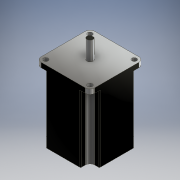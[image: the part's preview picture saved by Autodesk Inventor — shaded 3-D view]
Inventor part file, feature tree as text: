
AUTODESK INVENTOR PART (.ipt)
format: ipt  version: 2017 (Build 210142000, 142)  size: 271,360 bytes
history: native  units: mm
features: extrude x6, sketch x6, projected_geometry x2
ambient origin geometry x8: Origin, YZ Plane, XZ Plane, XY Plane, X Axis, Y Axis, Z Axis, Center Point
bodies: Solid1 (feature_tree)
feature tree (14):
  extrude  "Extrusion1"  Depth=28.5mm
  extrude  "Extrusion2"  Depth=10.0mm
  extrude  "Extrusion3"  Depth=10.0mm
  extrude  "Extrusion4"  Depth=57.0mm
  extrude  "Extrusion5"  Depth=1.0mm TaperAngle=0.0deg
  extrude  "Extrusion6"  Depth=10.0mm TaperAngle=0.0deg
  sketch  "Sketch1"  dims[d2=28.5mm d3=28.5mm]
  sketch  "Sketch2"  dims[d4=10.0mm d5=10.0mm]
  projected_geometry  "Projected Loop1"
  sketch  "Sketch3"  dims[d6=10.0mm d7=10.0mm]
  projected_geometry  "Projected Loop2"
  sketch  "Sketch4"  dims[d8=57.0mm d9=57.0mm]
  sketch  "Sketch5"  dims[d10=1.0mm d11=15.0mm d12=0.0mm]
  sketch  "Sketch6"  dims[d13=46.0mm d14=0.0mm d15=10.0mm d16=0.0mm d17=57.0mm d18=10.0mm d19=10.0mm d20=10.0mm d21=10.0mm d22=28.5mm d23=5.0mm d24=5.0mm d25=5.0mm d26=5.0mm d27=5.0mm d28=0.0mm d29=6.3mm d30=20.0mm d31=0.0mm d33=16.0mm d34=0.0mm]
